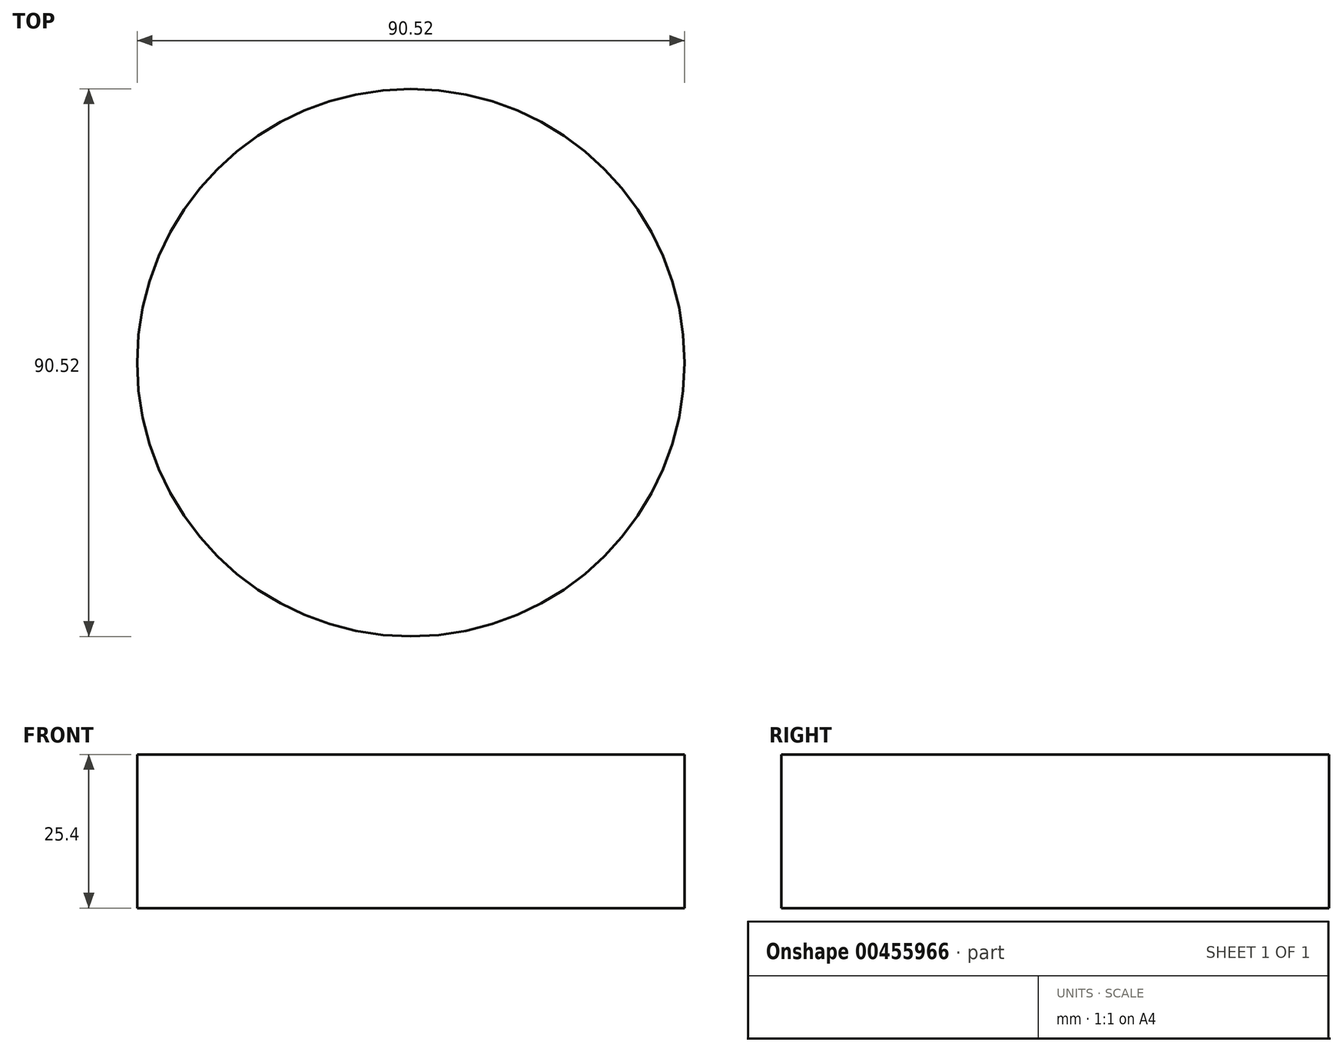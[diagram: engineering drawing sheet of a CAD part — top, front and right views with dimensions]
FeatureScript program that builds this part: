
annotation { "Feature Type Name" : "Feature", "Feature Type Description" : "" }
export const myFeature = defineFeature(function(context is Context, id is Id, definition is map)
    precondition{}
    {
        {
            var Q0;
            Q0=qCreatedBy(makeId("Top.planeOp"),FACE);
            var sketch = newSketch(context, id + "F0", { "sketchPlane" : qUnion([Q0])});
            skCircle(sketch, "E0", {"center": v(0, 0) * mm, "radius": 45.26 * mm});
            skSolve(sketch);
        }
        {
            var Q0;
            Q0 = qSketchRegion(id + "F0", true);
            extrude(context, id + "F1", {"entities" : qUnion([Q0]), "depth" : 25.4 * mm});
        }
    });
